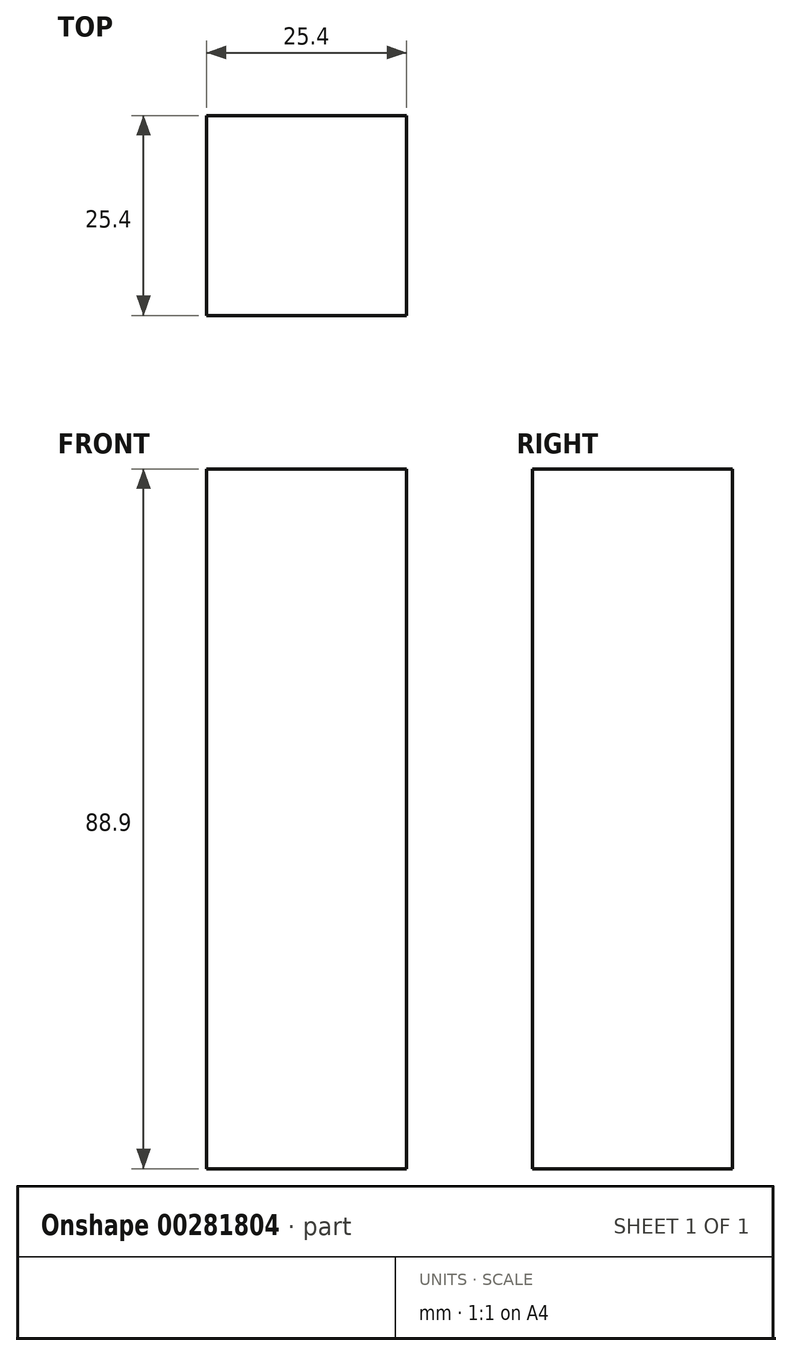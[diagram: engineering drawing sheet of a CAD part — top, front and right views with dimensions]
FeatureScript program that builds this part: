
annotation { "Feature Type Name" : "Feature", "Feature Type Description" : "" }
export const myFeature = defineFeature(function(context is Context, id is Id, definition is map)
    precondition{}
    {
        {
            var Q0;
            Q0=qCreatedBy(makeId("Front.planeOp"),FACE);
            var sketch = newSketch(context, id + "F0", { "sketchPlane" : qUnion([Q0])});
            skLineSegment(sketch, "E0.bottom", {"start": v(0, 0) * mm, "end": v(-25.4, 0) * mm});
            skLineSegment(sketch, "E0.top", {"start": v(0, 88.9) * mm, "end": v(-25.4, 88.9) * mm});
            skLineSegment(sketch, "E0.left", {"start": v(0, 0) * mm, "end": v(0, 88.9) * mm});
            skLineSegment(sketch, "E0.right", {"start": v(-25.4, 0) * mm, "end": v(-25.4, 88.9) * mm});
            skSolve(sketch);
        }
        {
            var Q0;
            Q0 = qSketchRegion(id + "F0", true);
            extrude(context, id + "F1", {"entities" : qUnion([Q0]), "depth" : 25.4 * mm});
        }
    });
